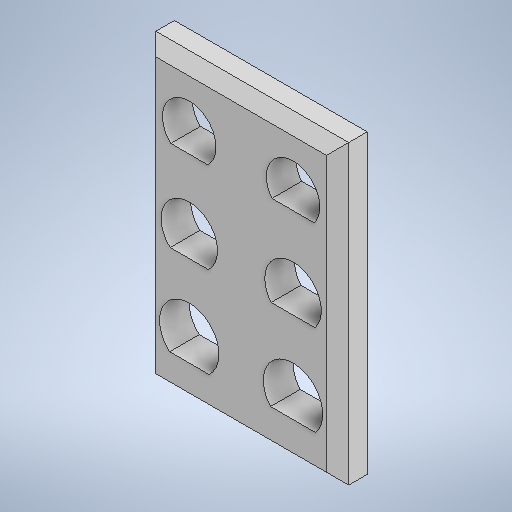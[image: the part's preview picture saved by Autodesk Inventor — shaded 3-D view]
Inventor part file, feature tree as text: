
AUTODESK INVENTOR PART (.ipt)
format: ipt  version: 2025.2 (Build 292293000, 293)  size: 299,520 bytes
history: native  units: in
note: dims shown in document units (in); Inventor stores cm internally (conversion verified against a paired STEP export)
features: sketch x8, extrude x5, hole x3, chamfer x1
ambient origin geometry x8: Origin, YZ Plane, XZ Plane, XY Plane, X Axis, Y Axis, Z Axis, Center Point
bodies: Solid1 (feature_tree)
feature tree (17):
  extrude  "Extrusion1"  Depth=0.7874in
  hole  "Hole3"  [1 undecoded]
  extrude  "Extrusion2"  Depth=0.0787in
  extrude  "Extrusion3"  Depth=0.1575in
  hole  "Hole4"  [1 undecoded]
  extrude  "Extrusion4"  Depth=0.0787in
  hole  "Hole5"  [1 undecoded]
  extrude  "Extrusion5"  Depth=0.0787in TaperAngle=0.0deg
  chamfer  "Chamfer1"  Distance=0.0433in
  sketch  "Sketch1"  dims[d0=0.5118in d1=0.7874in]
  sketch  "Sketch4"  dims[d2=0.3937in d3=0.3937in]
  sketch  "Sketch5"  dims[d4=0.0787in d5=0.0in d20=0.1575in]
  sketch  "Sketch6"  dims[d21=0.1181in d29=0.1575in]
  sketch  "Sketch7"  dims[d30=0.1417in d31=0.2362in d32=0.1575in d33=0.0787in d34=90.0deg d35=0.315in d36=0.8108in d37=0.1181in]
  sketch  "Sketch8"  dims[d38=0.1496in d39=0.2362in d40=0.1575in d41=0.0787in d42=90.0deg d43=0.315in d44=0.8108in d45=0.1181in]
  sketch  "Sketch9"  dims[d46=0.1575in d47=0.1575in]
  sketch  "Sketch10"  dims[d48=0.1575in d49=0.2362in d50=0.1575in d51=0.0787in d52=90.0deg d53=0.315in d54=0.8108in d56=0.0787in d57=0.0in d58=0.0433in d59=0.0787in d60=0.0in d61=0.0551in d62=0.0472in d63=0.0787in d64=0.0in d65=0.0591in d66=0.0512in d67=0.0787in d68=0.0in d69=0.0295in d70=0.0787in d71=45.0deg]
note: 3 required parameter values undecoded (feature->parameter linkage not recoverable at this tier; creation-order binding heuristic only, values carry confidence <= 0.55)
